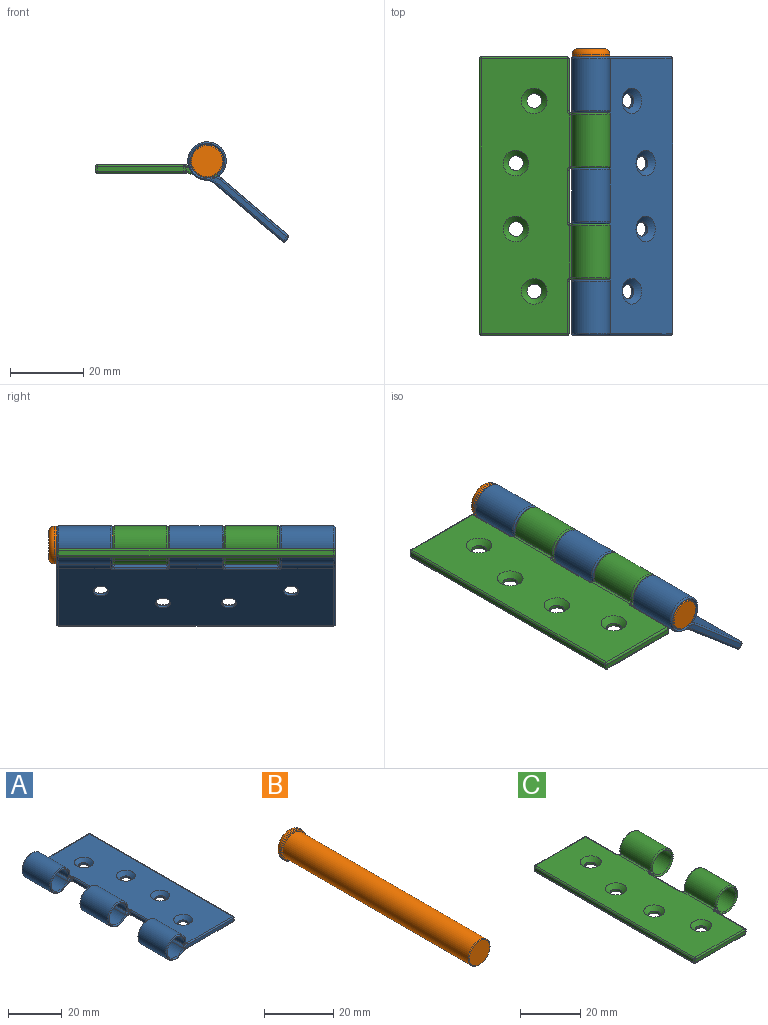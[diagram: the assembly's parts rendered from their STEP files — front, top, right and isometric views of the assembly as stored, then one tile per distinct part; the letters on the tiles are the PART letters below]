
ASSEMBLY  parts=3 mates=2
PART A: 94 faces, bbox 36.3x76x11.6 mm
  f0: cylinder r=5.25mm len=14.2mm, axis (0,1,0), area 412.4mm2, adj f2,f8,f69,f87
  f1: cylinder r=5.25mm len=14.2mm, axis (0,1,0), area 412.4mm2, adj f3,f9,f46,f78
  f2: plane 15.21x0.8mm, normal (0,0,-1), area 11.4mm2, adj f0,f4,f69,f71,f87,f90
  f3: plane 15.21x0.8mm, normal (0,0,-1), area 11.4mm2, adj f1,f5,f45,f46,f78,f80
  f4: cylinder r=4.5mm len=14.2mm, axis (0,1,0), area 382.9mm2, adj f2,f6,f71,f90
  f5: cylinder r=4.5mm len=14.2mm, axis (0,1,0), area 382.9mm2, adj f3,f7,f45,f80
  f6: cylinder r=2.39mm len=14.47mm, axis (0,1,0), area 36mm2, adj f4,f14,f73,f75,f92,f93
  f7: cylinder r=2.39mm len=14.33mm, axis (0,1,0), area 35.9mm2, adj f5,f14,f43,f82,f84
  f8: cylinder r=4.96mm len=14.47mm, axis (0,1,0), area 44.3mm2, adj f0,f16,f66,f68,f85,f88
  f9: cylinder r=4.96mm len=14.33mm, axis (0,1,0), area 44.3mm2, adj f1,f16,f48,f76,f77
  f10: cylinder r=5.25mm len=14.2mm, axis (0,1,0), area 412.4mm2, adj f11,f17,f51,f60
  f11: plane 15.21x0.8mm, normal (0,0,-1), area 11.4mm2, adj f10,f12,f51,f52,f60,f63
  f12: cylinder r=4.5mm len=14.2mm, axis (0,1,0), area 382.9mm2, adj f11,f13,f52,f63
  f13: cylinder r=2.39mm len=14.33mm, axis (0,1,0), area 35.9mm2, adj f12,f14,f49,f65,f67
  f14: plane 75x24mm, normal (0,0,1), area 1630.6mm2, adj f6,f7,f13,f21,f23,f25,f27,f41
  f15: plane 75x1.3mm, normal (1,0,0), area 97.5mm2, adj f38,f39,f42,f55
  f16: plane 75x24mm, normal (0,0,-1), area 1734.3mm2, adj f8,f9,f17,f20,f22,f24,f26,f50
  f17: cylinder r=4.96mm len=14.33mm, axis (0,1,0), area 44.3mm2, adj f10,f16,f54,f58,f61
  f18: plane 26.22x1.77mm, normal (0,-1,0), area 33.2mm2, adj f39,f47,f49,f52,f54,f56
  f19: plane 26.22x1.77mm, normal (0,1,0), area 33.2mm2, adj f38,f41,f43,f45,f48,f50
  f20: cylinder r=2mm len=4mm, axis (0,0,1), area 10.1mm2, adj f16,f21
  f21: cone r=2mm half-angle=45deg, axis (0,0,1), area 36.7mm2, adj f14,f20
  f22: cylinder r=2mm len=4mm, axis (0,0,1), area 10.1mm2, adj f16,f23
  f23: cone r=2mm half-angle=45deg, axis (0,0,1), area 36.7mm2, adj f14,f22
  f24: cylinder r=2mm len=4mm, axis (0,0,1), area 10.1mm2, adj f16,f25
  f25: cone r=2mm half-angle=45deg, axis (0,0,1), area 36.7mm2, adj f14,f24
  f26: cylinder r=2mm len=4mm, axis (0,0,1), area 10.1mm2, adj f16,f27
  f27: cone r=2mm half-angle=45deg, axis (0,0,1), area 36.7mm2, adj f14,f26
  f28: plane 14.2x1.3mm, normal (-1,0,0), area 18.5mm2, adj f34,f35,f81,f89
  f29: plane 1.72x1.7mm, normal (0,-1,0), area 1.3mm2, adj f34,f77,f80,f82
  f30: plane 1.72x1.7mm, normal (0,1,0), area 1.3mm2, adj f35,f88,f90,f92
  f31: plane 14.2x1.3mm, normal (-1,0,0), area 18.5mm2, adj f36,f37,f62,f72
  f32: plane 1.72x1.7mm, normal (0,1,0), area 1.3mm2, adj f36,f61,f63,f65
  f33: plane 1.72x1.7mm, normal (0,-1,0), area 1.3mm2, adj f37,f68,f71,f73
  f34: cylinder r=0.5mm len=1.32mm, axis (0,0,-1), area 1mm2, adj f28,f29,f76,f79,f84,f86
  f35: cylinder r=0.5mm len=1.32mm, axis (0,0,1), area 1mm2, adj f28,f30,f83,f85,f91,f93
  f36: cylinder r=0.5mm len=1.32mm, axis (0,0,-1), area 1mm2, adj f31,f32,f58,f59,f67,f70
  f37: cylinder r=0.5mm len=1.32mm, axis (0,0,1), area 1mm2, adj f31,f33,f64,f66,f74,f75
  f38: cylinder r=0.5mm len=1.3mm, axis (0,0,-1), area 1mm2, adj f15,f19,f40,f53
  f39: cylinder r=0.5mm len=1.3mm, axis (0,0,1), area 1mm2, adj f15,f18,f44,f57
  f40: sphere r=0.5mm, area 0.4mm2, adj f38,f41,f42
  f41: cylinder r=0.5mm len=24mm, axis (1,0,0), area 18.8mm2, adj f14,f19,f40,f43
  f42: cylinder r=0.5mm len=75mm, axis (0,1,0), area 58.9mm2, adj f14,f15,f40,f44
  f43: torus R=1.89mm, axis (0,-1,0), area 1.8mm2, adj f7,f19,f41,f45
  f44: sphere r=0.5mm, area 0.4mm2, adj f39,f42,f47
  f45: torus R=5mm, axis (0,-1,0), area 18.5mm2, adj f3,f5,f19,f43,f46,f48
  f46: torus R=4.75mm, axis (0,-1,0), area 18.7mm2, adj f1,f3,f45,f48
  f47: cylinder r=0.5mm len=24mm, axis (-1,0,0), area 18.8mm2, adj f14,f18,f44,f49
  f48: torus R=5.46mm, axis (0,-1,0), area 2.5mm2, adj f9,f19,f45,f46,f50
  f49: torus R=1.89mm, axis (0,-1,0), area 1.8mm2, adj f13,f18,f47,f52
  f50: cylinder r=0.5mm len=24mm, axis (-1,0,0), area 18.8mm2, adj f16,f19,f48,f53
  f51: torus R=4.75mm, axis (0,-1,0), area 18.7mm2, adj f10,f11,f52,f54
  f52: torus R=5mm, axis (0,-1,0), area 18.5mm2, adj f11,f12,f18,f49,f51,f54
  f53: sphere r=0.5mm, area 0.4mm2, adj f38,f50,f55
  f54: torus R=5.46mm, axis (0,-1,0), area 2.5mm2, adj f17,f18,f51,f52,f56
  f55: cylinder r=0.5mm len=75mm, axis (0,1,0), area 58.9mm2, adj f15,f16,f53,f57
  f56: cylinder r=0.5mm len=24mm, axis (1,0,0), area 18.8mm2, adj f16,f18,f54,f57
  f57: sphere r=0.5mm, area 0.4mm2, adj f39,f55,f56
  f58: bspline ~0.72x0.61mm, area 0.3mm2, adj f17,f36,f59,f61
  f59: torus R=1mm, axis (0,0,1), area 0.6mm2, adj f16,f36,f58,f62
  f60: torus R=4.75mm, axis (0,-1,0), area 18.7mm2, adj f10,f11,f61,f63
  f61: torus R=5.46mm, axis (0,-1,0), area 2.1mm2, adj f17,f32,f58,f60,f63
  f62: cylinder r=0.5mm len=14.2mm, axis (0,-1,0), area 11.2mm2, adj f16,f31,f59,f64
  f63: torus R=5mm, axis (0,-1,0), area 18.5mm2, adj f11,f12,f32,f60,f61,f65
  f64: torus R=1mm, axis (0,0,1), area 0.6mm2, adj f16,f37,f62,f66
  f65: torus R=1.89mm, axis (0,-1,0), area 1.4mm2, adj f13,f32,f63,f67
  f66: bspline ~0.72x0.61mm, area 0.3mm2, adj f8,f37,f64,f68
  f67: bspline ~0.83x0.6mm, area 0.3mm2, adj f13,f36,f65,f70
  f68: torus R=5.46mm, axis (0,-1,0), area 2.1mm2, adj f8,f33,f66,f69,f71
  f69: torus R=4.75mm, axis (0,-1,0), area 18.7mm2, adj f0,f2,f68,f71
  f70: torus R=1mm, axis (0,0,-1), area 0.6mm2, adj f14,f36,f67,f72
  f71: torus R=5mm, axis (0,-1,0), area 18.5mm2, adj f2,f4,f33,f68,f69,f73
  f72: cylinder r=0.5mm len=14.2mm, axis (0,-1,0), area 11.2mm2, adj f14,f31,f70,f74
  f73: torus R=1.89mm, axis (0,-1,0), area 1.4mm2, adj f6,f33,f71,f75
  f74: torus R=1mm, axis (0,0,-1), area 0.6mm2, adj f14,f37,f72,f75
  f75: bspline ~0.83x0.6mm, area 0.3mm2, adj f6,f37,f73,f74
  f76: bspline ~0.72x0.61mm, area 0.3mm2, adj f9,f34,f77,f79
  f77: torus R=5.46mm, axis (0,-1,0), area 2.1mm2, adj f9,f29,f76,f78,f80
  f78: torus R=4.75mm, axis (0,-1,0), area 18.7mm2, adj f1,f3,f77,f80
  f79: torus R=1mm, axis (0,0,1), area 0.6mm2, adj f16,f34,f76,f81
  f80: torus R=5mm, axis (0,-1,0), area 18.5mm2, adj f3,f5,f29,f77,f78,f82
  f81: cylinder r=0.5mm len=14.2mm, axis (0,1,0), area 11.2mm2, adj f16,f28,f79,f83
  f82: torus R=1.89mm, axis (0,-1,0), area 1.4mm2, adj f7,f29,f80,f84
  f83: torus R=1mm, axis (0,0,1), area 0.6mm2, adj f16,f35,f81,f85
  f84: bspline ~0.83x0.6mm, area 0.3mm2, adj f7,f34,f82,f86
  f85: bspline ~0.72x0.61mm, area 0.3mm2, adj f8,f35,f83,f88
  f86: torus R=1mm, axis (0,0,-1), area 0.6mm2, adj f14,f34,f84,f89
  f87: torus R=4.75mm, axis (0,-1,0), area 18.7mm2, adj f0,f2,f88,f90
  f88: torus R=5.46mm, axis (0,-1,0), area 2.1mm2, adj f8,f30,f85,f87,f90
  f89: cylinder r=0.5mm len=14.2mm, axis (0,-1,0), area 11.2mm2, adj f14,f28,f86,f91
  f90: torus R=5mm, axis (0,-1,0), area 18.5mm2, adj f2,f4,f30,f87,f88,f92
  f91: torus R=1mm, axis (0,0,-1), area 0.6mm2, adj f14,f35,f89,f93
  f92: torus R=1.89mm, axis (0,-1,0), area 1.4mm2, adj f6,f30,f90,f93
  f93: bspline ~0.83x0.6mm, area 0.3mm2, adj f6,f35,f91,f92
PART B: 8 faces, bbox 11x78.2x11 mm
  f0: cylinder r=4.4mm len=75.8mm, axis (0,1,0), area 2095.6mm2, adj f2,f5
  f1: plane 8.4x8.4mm, normal (0,-1,0), area 55.4mm2, adj f2
  f2: torus R=4.2mm, axis (0,-1,0), area 8.5mm2, adj f0,f1
  f3: cylinder r=5.1mm len=10.21mm, axis (0,-1,0), area 16mm2, adj f6,f7
  f4: plane 7.21x7.21mm, normal (0,1,0), area 40.8mm2, adj f6
  f5: plane 9.81x9.81mm, normal (0,-1,0), area 14.7mm2, adj f0,f7
  f6: torus R=3.6mm, axis (0,1,0), area 67.5mm2, adj f3,f4
  f7: torus R=4.9mm, axis (0,1,0), area 9.9mm2, adj f3,f5
PART C: 90 faces, bbox 36.3x76x11.6 mm
  f0: cylinder r=5.25mm len=14.2mm, axis (0,1,0), area 412.4mm2, adj f2,f8,f59,f83
  f1: cylinder r=5.25mm len=14.2mm, axis (0,1,0), area 412.4mm2, adj f3,f9,f46,f74
  f2: plane 15.21x0.8mm, normal (0,0,-1), area 11.4mm2, adj f0,f4,f59,f61,f83,f86
  f3: plane 15.21x0.8mm, normal (0,0,-1), area 11.4mm2, adj f1,f5,f46,f49,f74,f76
  f4: cylinder r=4.5mm len=14.2mm, axis (0,1,0), area 382.9mm2, adj f2,f6,f61,f86
  f5: cylinder r=4.5mm len=14.2mm, axis (0,1,0), area 382.9mm2, adj f3,f7,f49,f76
  f6: cylinder r=2.39mm len=14.47mm, axis (0,1,0), area 36mm2, adj f4,f10,f63,f65,f88,f89
  f7: cylinder r=2.39mm len=14.47mm, axis (0,1,0), area 36mm2, adj f5,f10,f51,f53,f78,f80
  f8: cylinder r=4.96mm len=14.47mm, axis (0,1,0), area 44.3mm2, adj f0,f12,f56,f58,f81,f84
  f9: cylinder r=4.96mm len=14.47mm, axis (0,1,0), area 44.3mm2, adj f1,f12,f44,f47,f72,f73
  f10: plane 75x24mm, normal (0,0,1), area 1623.5mm2, adj f6,f7,f16,f18,f20,f22,f55,f57
  f11: plane 75x1.3mm, normal (-1,0,0), area 97.5mm2, adj f36,f37,f43,f66
  f12: plane 75x24mm, normal (0,0,-1), area 1727.2mm2, adj f8,f9,f15,f17,f19,f21,f39,f40
  f13: plane 23.5x1.3mm, normal (0,-1,0), area 30.6mm2, adj f30,f37,f39,f62
  f14: plane 23.5x1.3mm, normal (0,1,0), area 30.6mm2, adj f34,f36,f48,f70
  f15: cylinder r=2mm len=4mm, axis (0,0,1), area 10.1mm2, adj f12,f16
  f16: cone r=2mm half-angle=45deg, axis (0,0,1), area 36.7mm2, adj f10,f15
  f17: cylinder r=2mm len=4mm, axis (0,0,1), area 10.1mm2, adj f12,f18
  f18: cone r=2mm half-angle=45deg, axis (0,0,1), area 36.7mm2, adj f10,f17
  f19: cylinder r=2mm len=4mm, axis (0,0,1), area 10.1mm2, adj f12,f20
  f20: cone r=2mm half-angle=45deg, axis (0,0,1), area 36.7mm2, adj f10,f19
  f21: cylinder r=2mm len=4mm, axis (0,0,1), area 10.1mm2, adj f12,f22
  f22: cone r=2mm half-angle=45deg, axis (0,0,1), area 36.7mm2, adj f10,f21
  f23: plane 14.2x1.3mm, normal (1,0,0), area 18.5mm2, adj f30,f31,f40,f57
  f24: plane 1.72x1.7mm, normal (0,-1,0), area 1.3mm2, adj f31,f47,f49,f51
  f25: plane 14.2x1.3mm, normal (1,0,0), area 18.5mm2, adj f32,f33,f77,f85
  f26: plane 1.72x1.7mm, normal (0,1,0), area 1.3mm2, adj f32,f73,f76,f78
  f27: plane 1.72x1.7mm, normal (0,-1,0), area 1.3mm2, adj f33,f84,f86,f88
  f28: plane 14.2x1.3mm, normal (1,0,0), area 18.5mm2, adj f34,f35,f52,f69
  f29: plane 1.72x1.7mm, normal (0,1,0), area 1.3mm2, adj f35,f58,f61,f63
  f30: cylinder r=0.5mm len=1.3mm, axis (0,0,1), area 1mm2, adj f13,f23,f38,f60
  f31: cylinder r=0.5mm len=1.32mm, axis (0,0,1), area 1mm2, adj f23,f24,f42,f44,f53,f55
  f32: cylinder r=0.5mm len=1.32mm, axis (0,0,-1), area 1mm2, adj f25,f26,f72,f75,f80,f82
  f33: cylinder r=0.5mm len=1.32mm, axis (0,0,1), area 1mm2, adj f25,f27,f79,f81,f87,f89
  f34: cylinder r=0.5mm len=1.3mm, axis (0,0,-1), area 1mm2, adj f14,f28,f50,f71
  f35: cylinder r=0.5mm len=1.32mm, axis (0,0,-1), area 1mm2, adj f28,f29,f54,f56,f65,f67
  f36: cylinder r=0.5mm len=1.3mm, axis (0,0,-1), area 1mm2, adj f11,f14,f45,f68
  f37: cylinder r=0.5mm len=1.3mm, axis (0,0,1), area 1mm2, adj f11,f13,f41,f64
  f38: sphere r=0.5mm, area 0.4mm2, adj f30,f39,f40
  f39: cylinder r=0.5mm len=23.5mm, axis (-1,0,0), area 18.5mm2, adj f12,f13,f38,f41
  f40: cylinder r=0.5mm len=14.2mm, axis (0,1,0), area 11.2mm2, adj f12,f23,f38,f42
  f41: sphere r=0.5mm, area 0.4mm2, adj f37,f39,f43
  f42: torus R=1mm, axis (0,0,1), area 0.6mm2, adj f12,f31,f40,f44
  f43: cylinder r=0.5mm len=75mm, axis (0,1,0), area 58.9mm2, adj f11,f12,f41,f45
  f44: bspline ~0.72x0.61mm, area 0.3mm2, adj f9,f31,f42,f47
  f45: sphere r=0.5mm, area 0.4mm2, adj f36,f43,f48
  f46: torus R=4.75mm, axis (0,1,0), area 18.7mm2, adj f1,f3,f47,f49
  f47: torus R=5.46mm, axis (0,1,0), area 2.1mm2, adj f9,f24,f44,f46,f49
  f48: cylinder r=0.5mm len=23.5mm, axis (1,0,0), area 18.5mm2, adj f12,f14,f45,f50
  f49: torus R=5mm, axis (0,1,0), area 18.5mm2, adj f3,f5,f24,f46,f47,f51
  f50: sphere r=0.5mm, area 0.4mm2, adj f34,f48,f52
  f51: torus R=1.89mm, axis (0,1,0), area 1.4mm2, adj f7,f24,f49,f53
  f52: cylinder r=0.5mm len=14.2mm, axis (0,-1,0), area 11.2mm2, adj f12,f28,f50,f54
  f53: bspline ~0.83x0.6mm, area 0.3mm2, adj f7,f31,f51,f55
  f54: torus R=1mm, axis (0,0,1), area 0.6mm2, adj f12,f35,f52,f56
  f55: torus R=1mm, axis (0,0,-1), area 0.6mm2, adj f10,f31,f53,f57
  f56: bspline ~0.72x0.61mm, area 0.3mm2, adj f8,f35,f54,f58
  f57: cylinder r=0.5mm len=14.2mm, axis (0,1,0), area 11.2mm2, adj f10,f23,f55,f60
  f58: torus R=5.46mm, axis (0,1,0), area 2.1mm2, adj f8,f29,f56,f59,f61
  f59: torus R=4.75mm, axis (0,1,0), area 18.7mm2, adj f0,f2,f58,f61
  f60: sphere r=0.5mm, area 0.4mm2, adj f30,f57,f62
  f61: torus R=5mm, axis (0,1,0), area 18.5mm2, adj f2,f4,f29,f58,f59,f63
  f62: cylinder r=0.5mm len=23.5mm, axis (1,0,0), area 18.5mm2, adj f10,f13,f60,f64
  f63: torus R=1.89mm, axis (0,1,0), area 1.4mm2, adj f6,f29,f61,f65
  f64: sphere r=0.5mm, area 0.4mm2, adj f37,f62,f66
  f65: bspline ~0.83x0.6mm, area 0.3mm2, adj f6,f35,f63,f67
  f66: cylinder r=0.5mm len=75mm, axis (0,1,0), area 58.9mm2, adj f10,f11,f64,f68
  f67: torus R=1mm, axis (0,0,-1), area 0.6mm2, adj f10,f35,f65,f69
  f68: sphere r=0.5mm, area 0.4mm2, adj f36,f66,f70
  f69: cylinder r=0.5mm len=14.2mm, axis (0,1,0), area 11.2mm2, adj f10,f28,f67,f71
  f70: cylinder r=0.5mm len=23.5mm, axis (-1,0,0), area 18.5mm2, adj f10,f14,f68,f71
  f71: sphere r=0.5mm, area 0.4mm2, adj f34,f69,f70
  f72: bspline ~0.72x0.61mm, area 0.3mm2, adj f9,f32,f73,f75
  f73: torus R=5.46mm, axis (0,1,0), area 2.1mm2, adj f9,f26,f72,f74,f76
  f74: torus R=4.75mm, axis (0,1,0), area 18.7mm2, adj f1,f3,f73,f76
  f75: torus R=1mm, axis (0,0,1), area 0.6mm2, adj f12,f32,f72,f77
  f76: torus R=5mm, axis (0,1,0), area 18.5mm2, adj f3,f5,f26,f73,f74,f78
  f77: cylinder r=0.5mm len=14.2mm, axis (0,1,0), area 11.2mm2, adj f12,f25,f75,f79
  f78: torus R=1.89mm, axis (0,1,0), area 1.4mm2, adj f7,f26,f76,f80
  f79: torus R=1mm, axis (0,0,1), area 0.6mm2, adj f12,f33,f77,f81
  f80: bspline ~0.83x0.6mm, area 0.3mm2, adj f7,f32,f78,f82
  f81: bspline ~0.72x0.61mm, area 0.3mm2, adj f8,f33,f79,f84
  f82: torus R=1mm, axis (0,0,-1), area 0.6mm2, adj f10,f32,f80,f85
  f83: torus R=4.75mm, axis (0,1,0), area 18.7mm2, adj f0,f2,f84,f86
  f84: torus R=5.46mm, axis (0,1,0), area 2.1mm2, adj f8,f27,f81,f83,f86
  f85: cylinder r=0.5mm len=14.2mm, axis (0,1,0), area 11.2mm2, adj f10,f25,f82,f87
  f86: torus R=5mm, axis (0,1,0), area 18.5mm2, adj f2,f4,f27,f83,f84,f88
  f87: torus R=1mm, axis (0,0,-1), area 0.6mm2, adj f10,f33,f85,f89
  f88: torus R=1.89mm, axis (0,1,0), area 1.4mm2, adj f6,f27,f86,f89
  f89: bspline ~0.83x0.6mm, area 0.3mm2, adj f6,f33,f87,f88
PLACE A rot(axis=(0,1,0),40.6deg) t=(8.42,-5.85,2)mm
PLACE B t=(7.63,-5.83,-2.14)mm
PLACE C t=(7.63,-5.88,-2.14)mm fixed
MATE revolute C.f0 <-> A.f0  axis (0,1,0) through (13.63,-66.66,-1.14)mm
MATE revolute B.f0 <-> A.f0  axis (0,-1,0) through (13.63,-81.83,-1.14)mm
